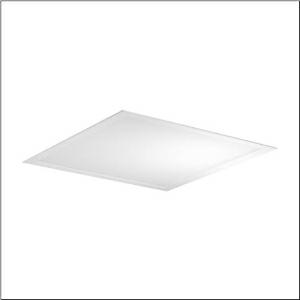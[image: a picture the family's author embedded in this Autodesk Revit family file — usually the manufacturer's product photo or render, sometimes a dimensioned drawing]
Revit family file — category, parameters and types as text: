
# Revit family: apollon_r__31_square_51mp11wd2m42_c9df
name_source: partatom
category: Lighting Fixtures
units: mm (PartAtom-declared; Revit-internal decimal feet)

## family parameters
Cut with Voids When Loaded = No
Host = Face
Light Source = No
Part Type = Normal
Room Calculation Point = No
Round Connector Dimension = Use Diameter
Shared = No

## types (1)
- --- (1 x LED, 4000 lm, 27.5 W, 4000K)
    Apparent Load = 28 VA
    CIE Flux Codes = 62 87 97 100 100
    Color Rendering = 80
    Color Temperature = 4000K
    Default Elevation = 1800 mm
    Description = Apollon® 31 square, office luminaire, primary optical cover: micro prismatic cover, of PMMA, CAT 2 (L<= 3000cd/m²), light emission: direct distribution, primary light characteristic: symmetric, installation type: lay-in mounting, LED, rated luminous flux: 4.000lm, luminous efficacy: 145lm/W, light colour: 830/840, colour temperature: 3000/4000K, control gear: DALI 2, Multilumen, with terminal, 5-pole, mains connection: 220..240V, AC/DC, 0/50..60Hz, rated input power: 28W, suitable for self-contained emergency lighting element 58DB00B013A with integrated self-test function according to EN 60598-2-22, housing, of aluminium, traffic white (RAL 9016), module: M625, length: 620mm, width: 620mm, height: 62mm, recess depth: 180mm, housing upper side, of sheet steel, coated, protection rating (complete): IP20, protection rating (on room side): IP40, insulation class (complete): insulation class II (safety insulation), certification: CE, ENEC, impact resistance: IK03, permissible operating ambient temperature: -20..+40°C, permissible storage temperature: -20..+60°C, standard: EN 60598-2-22, packaging unit: 1 piece
    Height = 0 mm  [stored 0 ft]
    Lamp = 1 x LED
    Lamp Light Flux = 4000 lm
    Lamp Power = 27.5 W
    Lamp count = 1
    Length = 620 mm
    Luminous efficacy = 145 lm/W
    Manufacturer = Siteco
    ModVariant = No
    Model = 51MP11WD2M42
    Mounting Place = Ceiling
    Mounting Type = Recessed
    Number of Poles = 1
    OnlyDefault = Yes
    Power Factor = 1
    Product Name = Apollon® 31 square
    Product group = office luminaire | ceiling recessed
    ProductGroupID = 400
    Protection Class = Protection class II
    Protection Degree = IP 20
    RLX_Detail_Level = 1
    RLX_Emergency_Light_Flux = 0 lm
    RLX_Emergency_Type = 0
    RLX_Emergency_Type_DB = No
    RlxData = <blob elided: 13421 chars, md5=3ea7ac0f>
    Socket = socket
    Standby Power = 0 W
    System Light Flux = 4000 lm
    System Power = 28 W
    Type Comments = factory setting: colour temperature 4000K
    Type Image = l_1291039.jpg
    URL = http://relux.com
    VarID = @adj_098153
    Voltage = 0 V
    Weight = 0.00 kg
    Width = 620 mm

note: [stored X ft] marks values corroborated as IEEE doubles in the binary element streams (Revit-internal decimal feet)

## geometry (parser evidence)
native form markers: Sweep x10
no freeform markers — native parametric forms only
